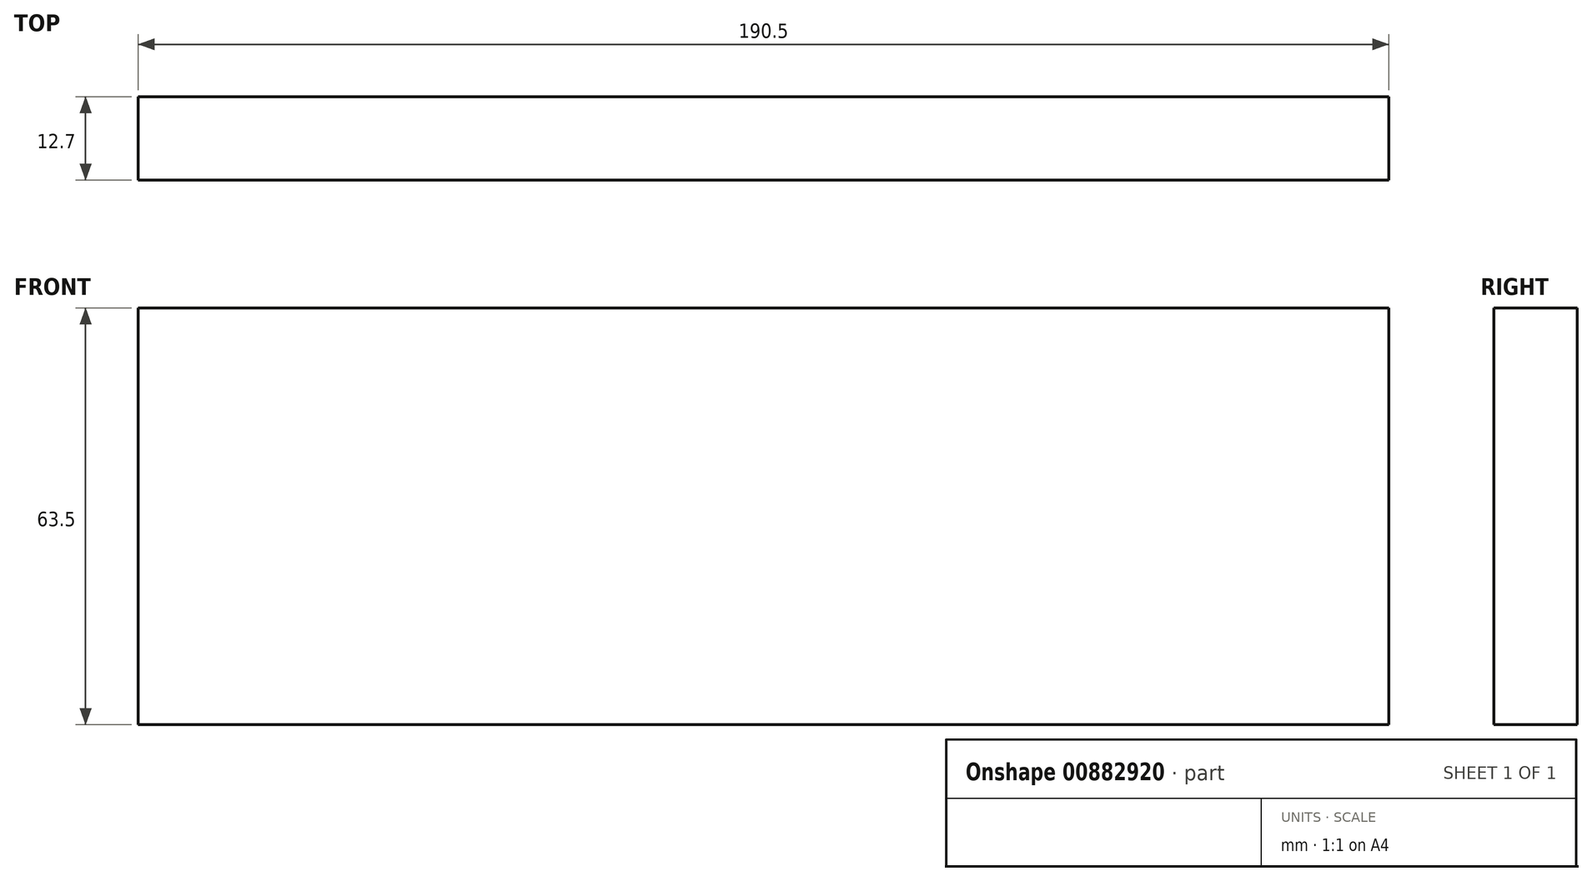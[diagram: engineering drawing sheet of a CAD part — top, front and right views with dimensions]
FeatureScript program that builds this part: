
annotation { "Feature Type Name" : "Feature", "Feature Type Description" : "" }
export const myFeature = defineFeature(function(context is Context, id is Id, definition is map)
    precondition{}
    {
        {
            var Q0;
            Q0=qCreatedBy(makeId("Front.planeOp"),FACE);
            var sketch = newSketch(context, id + "F0", { "sketchPlane" : qUnion([Q0])});
            skLineSegment(sketch, "E0.bottom", {"start": v(0, 0) * mm, "end": v(190.5, 0) * mm});
            skLineSegment(sketch, "E0.top", {"start": v(0, 63.5) * mm, "end": v(190.5, 63.5) * mm});
            skLineSegment(sketch, "E0.left", {"start": v(0, 0) * mm, "end": v(0, 63.5) * mm});
            skLineSegment(sketch, "E0.right", {"start": v(190.5, 0) * mm, "end": v(190.5, 63.5) * mm});
            skSolve(sketch);
        }
        {
            var Q0;
            Q0=makeQuery(id+"F0.imprint","IMPRINT",FACE,{"disambiguationData":[TD([[makeQuery(id+"F0.imprint","IMPRINT",EDGE,{"derivedFrom":sQuery(id+"F0.wireOp",EDGE,"E0.bottom")}),1.0]])]});
            extrude(context, id + "F1", {"entities" : qUnion([Q0]), "depth" : 12.7 * mm, "offsetDistance" : 25.4 * mm});
        }
    });
